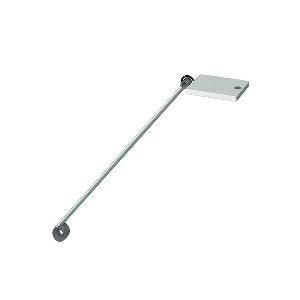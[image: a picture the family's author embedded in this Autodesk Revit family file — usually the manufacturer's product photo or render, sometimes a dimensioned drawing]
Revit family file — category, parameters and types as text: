
# Revit family: para_mi_-_mftl_108_r__940_00644014_f05d
name_source: partatom
category: Lighting Fixtures
units: mm (PartAtom-declared; Revit-internal decimal feet)

## family parameters
Cut with Voids When Loaded = No
Host = Face
Light Source = No
Part Type = Normal
Room Calculation Point = No
Round Connector Dimension = Use Diameter
Shared = No

## types (1)
- PARA.MI - MFTL 108 R /940 (1 x LED, 600 lm, 4000K)
    Apparent Load = 7 VA
    Approval mark = CE
    CIE Flux Codes = 70 94 99 100 100
    Color Rendering = 90-100
    Color Temperature = 4000K
    Control Gear = Electronic ballast
    Default Elevation = 1800 mm
    Description = MFTL 108 R|Task luminaire|light source: LED|work equipment: Electronic plug-in transformer|connected load: 100-240 V, 50/60 Hz|Power consumption: approx. 7 W|luminous flux: 600 lm|luminous efficacy: 85 lm/W|Illuminance efficiency factor: 111 lx/W|colour temperature: Cold white, ca. 4000 K|color rendering index (CRI): >= 90|chromaticity tolerance:  3 SDCM|class of protection: II with plug-in power supply, III without plug-in power supply|technology: Continuously dimmable|luminaire body|material: Aluminium|surface: Painted|colour: Silver|lamp cover: Plastic, Clear|tubular sections|material: Tubular aluminium section|surface: Painted|colour: Silver metallic|weight (net): approx. 0.8 kg|mains lead: 3.00 m Mains plug BS 1363, CEE 7/XVI, NEMA 1-15P|Fastening: Adaptor (accessory), Table base (accessory), Table clamp (accessory), Tap16|glare control: Reflector|special features: Automatic switchoff adjustable, Push button in luminaire head, Behaviour at net recovery adjustable|Approval mark: C - ETL - US (F. CAN U. USA), VDE - ENEC SEP LIGHT & POWER SUPPLY UNIT|
    Height = 12 mm  [stored 0.0393701 ft]
    Lamp = 1 x LED
    Lamp Light Flux = 600 lm
    Lamp count = 1
    Length = 123 mm
    Luminous efficacy = 86 lm/W
    Manufacturer = Waldmann
    ModVariant = No
    Model = 00644014
    Mounting Place = Table
    Mounting Type = Surface mounted
    Number of Poles = 1
    OnlyDefault = Yes
    Power Factor = 1
    Product Name = PARA.MI - MFTL 108 R /940
    Product group = Task luminaire (office)
    ProductGroupID = 21
    Protection Class = Protection class II
    Protection Degree = IP 40
    RLX_Detail_Level = 1
    RLX_Emergency_Light_Flux = 0 lm
    RLX_Emergency_Type = 0
    RLX_Emergency_Type_DB = No
    RlxData = <blob elided: 53025 chars, md5=8134baac>
    Socket = socket
    Standby Power = 0 W
    System Light Flux = 600 lm
    System Power = 7 W
    Type Comments = Product without accessories
    Type Image = 113149000-00644014.jpg
    URL = http://relux.com
    VarID = ---
    Voltage = 230 V
    Voltage Range = 220-240 V
    Weight = 0.00 kg
    Width = 0 mm  [stored 0 ft]

note: [stored X ft] marks values corroborated as IEEE doubles in the binary element streams (Revit-internal decimal feet)

## geometry (parser evidence)
native form markers: Blend x4, Sweep x12
no freeform markers — native parametric forms only
